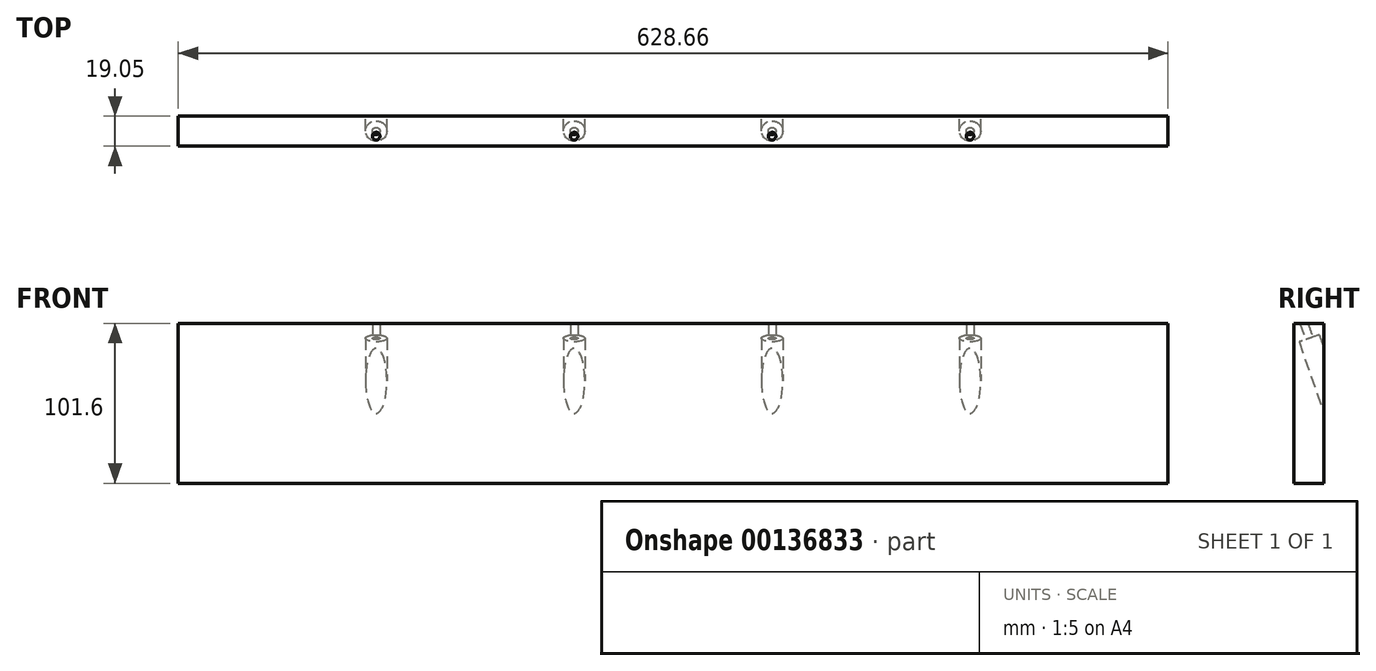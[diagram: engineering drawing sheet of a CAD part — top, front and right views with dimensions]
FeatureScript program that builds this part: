
annotation { "Feature Type Name" : "Feature", "Feature Type Description" : "" }
export const myFeature = defineFeature(function(context is Context, id is Id, definition is map)
    precondition{}
    {
        {
            var Q0;
            Q0=qCreatedBy(makeId("Front.planeOp"),FACE);
            var sketch = newSketch(context, id + "F0", { "sketchPlane" : qUnion([Q0])});
            skLineSegment(sketch, "E0.bottom", {"start": v(314.32, -50.8) * mm, "end": v(-314.33, -50.8) * mm});
            skLineSegment(sketch, "E0.top", {"start": v(314.33, 50.8) * mm, "end": v(-314.33, 50.8) * mm});
            skLineSegment(sketch, "E0.left", {"start": v(314.33, -50.8) * mm, "end": v(314.33, 50.8) * mm});
            skLineSegment(sketch, "E0.right", {"start": v(-314.33, -50.8) * mm, "end": v(-314.33, 50.8) * mm});
            skPoint(sketch, "E0.middle", {"position": v(0, 0) * mm});
            skSolve(sketch);
        }
        {
            var Q0;
            Q0=makeQuery(id+"F0.imprint","IMPRINT",FACE,{"disambiguationData":[TD([[makeQuery(id+"F0.imprint","IMPRINT",EDGE,{"derivedFrom":sQuery(id+"F0.wireOp",EDGE,"E0.bottom")}),-1.0]])]});
            extrude(context, id + "F1", {"entities" : qUnion([Q0]), "oppositeDirection" : true, "depth" : 19.05 * mm});
        }
        {
            var Q0;
            Q0=qCreatedBy(makeId("Right.planeOp"),FACE);
            var sketch = newSketch(context, id + "F2", { "sketchPlane" : qUnion([Q0])});
            skLineSegment(sketch, "E1", {"start": v(-29.87, -12.8) * mm, "end": v(-19.57, -9.22) * mm});
            skLineSegment(sketch, "E2", {"start": v(38.16, 13.38) * mm, "end": v(-38.16, -13.17) * mm});
            skLineSegment(sketch, "E3", {"start": v(-19.57, -9.22) * mm, "end": v(-18.12, -13.38) * mm});
            skLineSegment(sketch, "E4", {"start": v(27.28, 2.41) * mm, "end": v(-18.12, -13.38) * mm});
            skLineSegment(sketch, "E5", {"start": v(25.05, 8.82) * mm, "end": v(27.28, 2.41) * mm});
            skLineSegment(sketch, "E6", {"start": v(-29.87, -12.8) * mm, "end": v(-30.66, -10.56) * mm});
            skLineSegment(sketch, "E7", {"start": v(-29.87, -10.29) * mm, "end": v(-29.87, 2.41) * mm});
            skLineSegment(sketch, "E8", {"start": v(-29.87, 2.41) * mm, "end": v(6.64, 2.41) * mm});
            skSolve(sketch);
        }
        {
            var Q0;
            Q0=makeQuery(id+"F2.imprint","IMPRINT",FACE,{"disambiguationData":[TD([[makeQuery(id+"F2.imprint","IMPRINT",EDGE,{"derivedFrom":sQuery(id+"F2.wireOp",EDGE,"E1")}),1.0]])]});
            var Q1;
            Q1=sQuery(id+"F2.wireOp",EDGE,"E2");
            revolve(context, id + "F3", {"entities" : qUnion([Q0]), "axis" : qUnion([Q1]), "revolveType" : RevolveType.FULL});
        }
        {
            var Q0;
            Q0=makeQuery(id+"F1.opExtrude","SWEPT_FACE",FACE,{"disambiguationData":[OSD([sQuery(id+"F0.wireOp",EDGE,"E0.top")])]});
            var sketch = newSketch(context, id + "F4", { "sketchPlane" : qUnion([Q0])});
            skLineSegment(sketch, "E9.0", {"start": v(314.33, 19.05) * mm, "end": v(-314.33, 19.05) * mm, "construction": true});
            skPoint(sketch, "E10", {"position": v(-188.6, 19.05) * mm});
            skPoint(sketch, "E11", {"position": v(-62.87, 19.05) * mm});
            skPoint(sketch, "E12", {"position": v(62.87, 19.05) * mm});
            skPoint(sketch, "E13", {"position": v(188.6, 19.05) * mm});
            skSolve(sketch);
        }
        {
            var Q0;
            Q0=makeQuery(id+"F3.opRevolve","SWEPT_BODY",BODY,{"disambiguationData":[OSD([sQuery(id+"F2.wireOp",EDGE,"E1"),sQuery(id+"F2.wireOp",EDGE,"E2"),sQuery(id+"F2.wireOp",EDGE,"E3"),sQuery(id+"F2.wireOp",EDGE,"E4"),sQuery(id+"F2.wireOp",EDGE,"E5"),sQuery(id+"F2.wireOp",EDGE,"E6")])]});
            var Q1;
            Q1=sQuery(id+"F2.wireOp",VERTEX,"E8.start");
            var Q2;
            Q2=sQuery(id+"F4.wireOp",VERTEX,"E10");
            transform(context, id + "F5", {"entities" : qUnion([Q0]), "transformType" : TransformType.TRANSLATION_ENTITY, "oppositeDirectionEntity" : false, "transformLine" : qUnion([Q1, Q2]), "makeCopy" : true});
        }
        {
            var Q0;
            Q0=makeQuery(id+"F5.opPattern","COPY",BODY,{"derivedFrom":makeQuery(id+"F3.opRevolve","SWEPT_BODY",BODY,{"disambiguationData":[OSD([sQuery(id+"F2.wireOp",EDGE,"E1"),sQuery(id+"F2.wireOp",EDGE,"E2"),sQuery(id+"F2.wireOp",EDGE,"E3"),sQuery(id+"F2.wireOp",EDGE,"E4"),sQuery(id+"F2.wireOp",EDGE,"E5"),sQuery(id+"F2.wireOp",EDGE,"E6")])]}),"instanceName":"1"});
            var Q1;
            Q1=makeQuery(id+"F1.opExtrude","CAP_EDGE",EDGE,{"disambiguationData":[OSD([sQuery(id+"F0.wireOp",EDGE,"E0.top")])],"isStart":false});
            transform(context, id + "F6", {"entities" : qUnion([Q0]), "transformType" : TransformType.ROTATION, "transformAxis" : qUnion([Q1]), "angle" : 90 * degree, "makeCopy" : false});
        }
        {
            var Q0;
            Q0=makeQuery(id+"F3.opRevolve","SWEPT_BODY",BODY,{"disambiguationData":[OSD([sQuery(id+"F2.wireOp",EDGE,"E1"),sQuery(id+"F2.wireOp",EDGE,"E2"),sQuery(id+"F2.wireOp",EDGE,"E3"),sQuery(id+"F2.wireOp",EDGE,"E4"),sQuery(id+"F2.wireOp",EDGE,"E5"),sQuery(id+"F2.wireOp",EDGE,"E6")])]});
            var Q1;
            Q1=sQuery(id+"F2.wireOp",VERTEX,"E8.start");
            var Q2;
            Q2=sQuery(id+"F4.wireOp",VERTEX,"E11");
            transform(context, id + "F7", {"entities" : qUnion([Q0]), "transformType" : TransformType.TRANSLATION_ENTITY, "oppositeDirectionEntity" : false, "transformLine" : qUnion([Q1, Q2]), "makeCopy" : true});
        }
        {
            var Q0;
            Q0=makeQuery(id+"F3.opRevolve","SWEPT_BODY",BODY,{"disambiguationData":[OSD([sQuery(id+"F2.wireOp",EDGE,"E1"),sQuery(id+"F2.wireOp",EDGE,"E2"),sQuery(id+"F2.wireOp",EDGE,"E3"),sQuery(id+"F2.wireOp",EDGE,"E4"),sQuery(id+"F2.wireOp",EDGE,"E5"),sQuery(id+"F2.wireOp",EDGE,"E6")])]});
            var Q1;
            Q1=sQuery(id+"F2.wireOp",VERTEX,"E8.start");
            var Q2;
            Q2=sQuery(id+"F4.wireOp",VERTEX,"E12");
            transform(context, id + "F8", {"entities" : qUnion([Q0]), "transformType" : TransformType.TRANSLATION_ENTITY, "oppositeDirectionEntity" : false, "transformLine" : qUnion([Q1, Q2]), "makeCopy" : true});
        }
        {
            var Q0;
            Q0=makeQuery(id+"F3.opRevolve","SWEPT_BODY",BODY,{"disambiguationData":[OSD([sQuery(id+"F2.wireOp",EDGE,"E1"),sQuery(id+"F2.wireOp",EDGE,"E2"),sQuery(id+"F2.wireOp",EDGE,"E3"),sQuery(id+"F2.wireOp",EDGE,"E4"),sQuery(id+"F2.wireOp",EDGE,"E5"),sQuery(id+"F2.wireOp",EDGE,"E6")])]});
            var Q1;
            Q1=sQuery(id+"F2.wireOp",VERTEX,"E8.start");
            var Q2;
            Q2=sQuery(id+"F4.wireOp",VERTEX,"E13");
            transform(context, id + "F9", {"entities" : qUnion([Q0]), "transformType" : TransformType.TRANSLATION_ENTITY, "oppositeDirectionEntity" : false, "transformLine" : qUnion([Q1, Q2]), "makeCopy" : false});
        }
        {
            var Q0;
            Q0=makeQuery(id+"F7.opPattern","COPY",BODY,{"derivedFrom":makeQuery(id+"F3.opRevolve","SWEPT_BODY",BODY,{"disambiguationData":[OSD([sQuery(id+"F2.wireOp",EDGE,"E1"),sQuery(id+"F2.wireOp",EDGE,"E2"),sQuery(id+"F2.wireOp",EDGE,"E3"),sQuery(id+"F2.wireOp",EDGE,"E4"),sQuery(id+"F2.wireOp",EDGE,"E5"),sQuery(id+"F2.wireOp",EDGE,"E6")])]}),"instanceName":"1"});
            var Q1;
            Q1=makeQuery(id+"F8.opPattern","COPY",BODY,{"derivedFrom":makeQuery(id+"F3.opRevolve","SWEPT_BODY",BODY,{"disambiguationData":[OSD([sQuery(id+"F2.wireOp",EDGE,"E1"),sQuery(id+"F2.wireOp",EDGE,"E2"),sQuery(id+"F2.wireOp",EDGE,"E3"),sQuery(id+"F2.wireOp",EDGE,"E4"),sQuery(id+"F2.wireOp",EDGE,"E5"),sQuery(id+"F2.wireOp",EDGE,"E6")])]}),"instanceName":"1"});
            var Q2;
            Q2=makeQuery(id+"F3.opRevolve","SWEPT_BODY",BODY,{"disambiguationData":[OSD([sQuery(id+"F2.wireOp",EDGE,"E1"),sQuery(id+"F2.wireOp",EDGE,"E2"),sQuery(id+"F2.wireOp",EDGE,"E3"),sQuery(id+"F2.wireOp",EDGE,"E4"),sQuery(id+"F2.wireOp",EDGE,"E5"),sQuery(id+"F2.wireOp",EDGE,"E6")])]});
            var Q3;
            Q3=sQuery(id+"F4.wireOp",EDGE,"E9.0");
            transform(context, id + "F10", {"entities" : qUnion([Q0, Q1, Q2]), "transformType" : TransformType.ROTATION, "transformAxis" : qUnion([Q3]), "angle" : 90 * degree, "makeCopy" : false});
        }
        {
            var Q0;
            Q0=makeQuery(id+"F5.opPattern","COPY",BODY,{"derivedFrom":makeQuery(id+"F3.opRevolve","SWEPT_BODY",BODY,{"disambiguationData":[OSD([sQuery(id+"F2.wireOp",EDGE,"E1"),sQuery(id+"F2.wireOp",EDGE,"E2"),sQuery(id+"F2.wireOp",EDGE,"E3"),sQuery(id+"F2.wireOp",EDGE,"E4"),sQuery(id+"F2.wireOp",EDGE,"E5"),sQuery(id+"F2.wireOp",EDGE,"E6")])]}),"instanceName":"1"});
            var Q1;
            Q1=makeQuery(id+"F7.opPattern","COPY",BODY,{"derivedFrom":makeQuery(id+"F3.opRevolve","SWEPT_BODY",BODY,{"disambiguationData":[OSD([sQuery(id+"F2.wireOp",EDGE,"E1"),sQuery(id+"F2.wireOp",EDGE,"E2"),sQuery(id+"F2.wireOp",EDGE,"E3"),sQuery(id+"F2.wireOp",EDGE,"E4"),sQuery(id+"F2.wireOp",EDGE,"E5"),sQuery(id+"F2.wireOp",EDGE,"E6")])]}),"instanceName":"1"});
            var Q2;
            Q2=makeQuery(id+"F8.opPattern","COPY",BODY,{"derivedFrom":makeQuery(id+"F3.opRevolve","SWEPT_BODY",BODY,{"disambiguationData":[OSD([sQuery(id+"F2.wireOp",EDGE,"E1"),sQuery(id+"F2.wireOp",EDGE,"E2"),sQuery(id+"F2.wireOp",EDGE,"E3"),sQuery(id+"F2.wireOp",EDGE,"E4"),sQuery(id+"F2.wireOp",EDGE,"E5"),sQuery(id+"F2.wireOp",EDGE,"E6")])]}),"instanceName":"1"});
            var Q3;
            Q3=makeQuery(id+"F3.opRevolve","SWEPT_BODY",BODY,{"disambiguationData":[OSD([sQuery(id+"F2.wireOp",EDGE,"E1"),sQuery(id+"F2.wireOp",EDGE,"E2"),sQuery(id+"F2.wireOp",EDGE,"E3"),sQuery(id+"F2.wireOp",EDGE,"E4"),sQuery(id+"F2.wireOp",EDGE,"E5"),sQuery(id+"F2.wireOp",EDGE,"E6")])]});
            var Q4;
            Q4=makeQuery(id+"F1.opExtrude","SWEPT_BODY",BODY,{"disambiguationData":[OSD([sQuery(id+"F0.wireOp",EDGE,"E0.bottom"),sQuery(id+"F0.wireOp",EDGE,"E0.top"),sQuery(id+"F0.wireOp",EDGE,"E0.left"),sQuery(id+"F0.wireOp",EDGE,"E0.right")])]});
            booleanBodies(context, id + "F11", {"operationType" : BooleanOperationType.SUBTRACTION, "tools" : qUnion([Q0, Q1, Q2, Q3]), "targets" : qUnion([Q4])});
        }
    });
